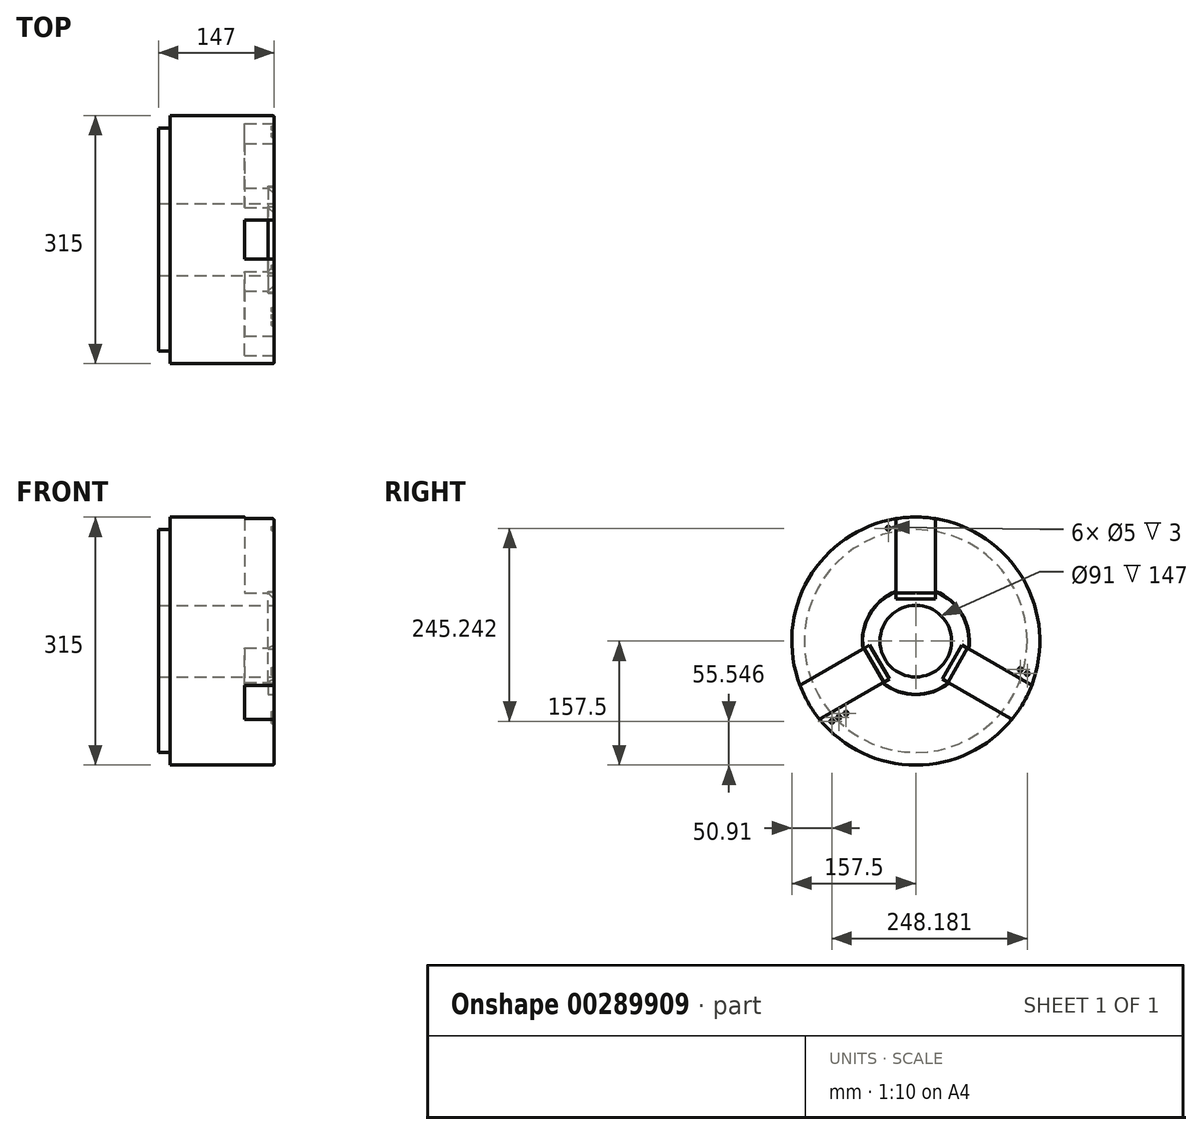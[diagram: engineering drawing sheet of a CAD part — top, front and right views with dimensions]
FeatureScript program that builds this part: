
annotation { "Feature Type Name" : "Feature", "Feature Type Description" : "" }
export const myFeature = defineFeature(function(context is Context, id is Id, definition is map)
    precondition{}
    {
        {
            var Q0;
            Q0=qCreatedBy(makeId("Front.planeOp"),FACE);
            var sketch = newSketch(context, id + "F0", { "sketchPlane" : qUnion([Q0])});
            skLineSegment(sketch, "E0", {"start": v(0, 45.5) * mm, "end": v(0, 67.5) * mm});
            skLineSegment(sketch, "E1", {"start": v(-2, 157.5) * mm, "end": v(-132, 157.5) * mm});
            skLineSegment(sketch, "E2", {"start": v(-132, 157.5) * mm, "end": v(-132, 141.5) * mm});
            skLineSegment(sketch, "E3", {"start": v(-132, 141.5) * mm, "end": v(-147, 141.5) * mm});
            skLineSegment(sketch, "E4", {"start": v(-147, 141.5) * mm, "end": v(-147, 45.5) * mm});
            skLineSegment(sketch, "E5", {"start": v(-147, 45.5) * mm, "end": v(0, 45.5) * mm});
            skLineSegment(sketch, "E6", {"start": v(294.82, 0) * mm, "end": v(-412.28, 0) * mm, "construction": true});
            skPoint(sketch, "E7.visualSharp", {"position": v(0, 157.5) * mm});
            skArc(sketch, "E7.filletArc", {"start": v(0, 155.5) * mm, "mid": v(-0.59, 156.91) * mm, "end": v(-2, 157.5) * mm});
            skLineSegment(sketch, "E8.bottom", {"start": v(0, 67.5) * mm, "end": v(-8, 67.5) * mm});
            skLineSegment(sketch, "E8.top", {"start": v(0, 68) * mm, "end": v(-8, 68) * mm});
            skLineSegment(sketch, "E8.right", {"start": v(-8, 67.5) * mm, "end": v(-8, 68) * mm});
            skLineSegment(sketch, "E9.trimOffspring", {"start": v(0, 68) * mm, "end": v(0, 155.5) * mm});
            skSolve(sketch);
        }
        {
            var Q0;
            Q0=qSketchRegion(id+"F0",true);
            var Q1;
            Q1=sQuery(id+"F0.wireOp",EDGE,"E6");
            revolve(context, id + "F1", {"entities" : qUnion([Q0]), "axis" : qUnion([Q1]), "revolveType" : RevolveType.FULL});
        }
        {
            var Q0;
            Q0=makeQuery(id+"F1.opRevolve","SWEPT_FACE",FACE,{"disambiguationData":[OSD([sQuery(id+"F0.wireOp",EDGE,"E0")])]});
            var sketch = newSketch(context, id + "F2", { "sketchPlane" : qUnion([Q0])});
            skLineSegment(sketch, "E10", {"start": v(0, 0) * mm, "end": v(0, 187.03) * mm, "construction": true});
            skArc(sketch, "E11", {"start": v(25, 155.5) * mm, "mid": v(0, 157.5) * mm, "end": v(-25, 155.5) * mm});
            skPoint(sketch, "E12", {"position": v(0, 62.16) * mm});
            skLineSegment(sketch, "E13", {"start": v(25, 155.5) * mm, "end": v(25, 60.5) * mm});
            skLineSegment(sketch, "E14", {"start": v(25, 60.5) * mm, "end": v(-25, 60.5) * mm});
            skLineSegment(sketch, "E15", {"start": v(-25, 60.5) * mm, "end": v(-25, 155.5) * mm});
            skSolve(sketch);
        }
        {
            var Q0;
            {var subQ0=sQuery(id+"F2.wireOp",EDGE,"E11");Q0=makeQuery(id+"F2.imprint","IMPRINT",FACE,{"disambiguationData":[TD([[makeQuery(id+"F2.imprint","IMPRINT",EDGE,{"derivedFrom":subQ0}),1.0]])]});}
            var Q1;
            {var subQ0=sQuery(id+"F2.wireOp",EDGE,"LmhPQE9t-ctvD-aCPM-Uwr9-EQLkLqq6skGc.bottom");Q1=makeQuery(id+"F2.imprint","IMPRINT",FACE,{"disambiguationData":[TD([[makeQuery(id+"F2.imprint","IMPRINT",EDGE,{"derivedFrom":subQ0}),-1.0]])]});}
            var Q2;
            {var subQ0=sQuery(id+"F2.wireOp",EDGE,"LmhPQE9t-ctvD-aCPM-Uwr9-EQLkLqq6skGc.bottom");var subQ1=makeQuery(id+"F1.opRevolve","SWEPT_EDGE",EDGE,{"disambiguationData":[OSD([sQuery(id+"F0.wireOp",EDGE,"E0"),sQuery(id+"F0.wireOp",EDGE,"E8.bottom")])]});var subQ2=makeQuery(id+"F2.imprint","INTERSECT",VERTEX,{"disambiguationData":[OD(0.0)],"derivedFrom":[subQ1,subQ0]});Q2=makeQuery(id+"F2.imprint","IMPRINT",FACE,{"disambiguationData":[TD([[makeQuery(id+"F2.imprint","IMPRINT",EDGE,{"disambiguationData":[TD([[subQ2,-1.0]])],"derivedFrom":subQ0}),-1.0]])]});}
            extrude(context, id + "F3", {"entities" : qUnion([Q0, Q1, Q2]), "operationType" : NewBodyOperationType.REMOVE, "oppositeDirection" : true, "depth" : 37.5 * mm});
        }
        {
            var Q0;
            Q0=makeQuery(id+"F1.opRevolve","SWEPT_FACE",FACE,{"disambiguationData":[OSD([sQuery(id+"F0.wireOp",EDGE,"E0")])]});
            var sketch = newSketch(context, id + "F4", { "sketchPlane" : qUnion([Q0])});
            skLineSegment(sketch, "E16", {"start": v(25, 73.3) * mm, "end": v(-25, 73.3) * mm});
            skLineSegment(sketch, "E17", {"start": v(-25, 73.3) * mm, "end": v(-25, 53.3) * mm});
            skLineSegment(sketch, "E18", {"start": v(-25, 53.3) * mm, "end": v(25, 53.3) * mm});
            skLineSegment(sketch, "E19", {"start": v(25, 53.3) * mm, "end": v(25, 73.3) * mm});
            skSolve(sketch);
        }
        {
            var Q0;
            Q0=qSketchRegion(id+"F4",true);
            extrude(context, id + "F5", {"entities" : qUnion([Q0]), "operationType" : NewBodyOperationType.REMOVE, "oppositeDirection" : true, "depth" : 8 * mm});
        }
        {
            var Q0;
            Q0=makeQuery(id+"F5.boolean.opBoolean","COPY",EDGE,{"derivedFrom":makeQuery(id+"F5.opExtrude","CAP_EDGE",EDGE,{"disambiguationData":[OSD([sQuery(id+"F4.wireOp",EDGE,"E18")])],"isStart":false})});
            chamfer(context, id + "F6", {"entities" : qUnion([Q0]), "width" : 8 * mm, "tangentPropagation" : true});
        }
        {
            var Q0;
            Q0=makeQuery(id+"F5.boolean.opBoolean","COPY",FACE,{"derivedFrom":makeQuery(id+"F5.opExtrude","CAP_FACE",FACE,{"disambiguationData":[OSD([sQuery(id+"F4.wireOp",EDGE,"E16"),sQuery(id+"F4.wireOp",EDGE,"E17"),sQuery(id+"F4.wireOp",EDGE,"E18"),sQuery(id+"F4.wireOp",EDGE,"E19")])],"isStart":false})});
            var Q1;
            Q1=makeQuery(id+"F3.boolean.opBoolean","COPY",FACE,{"derivedFrom":makeQuery(id+"F3.opExtrude","CAP_FACE",FACE,{"disambiguationData":[OSD([sQuery(id+"F0.wireOp",EDGE,"E0"),sQuery(id+"F0.wireOp",EDGE,"E8.bottom"),sQuery(id+"F2.wireOp",EDGE,"E11"),sQuery(id+"F2.wireOp",EDGE,"E13"),sQuery(id+"F2.wireOp",EDGE,"E15")])],"isStart":false})});
            extrude(context, id + "F7", {"entities" : qUnion([Q0]), "operationType" : NewBodyOperationType.REMOVE, "endBound" : BoundingType.UP_TO_SURFACE, "oppositeDirection" : true, "endBoundEntityFace" : qUnion([Q1]), "depth" : 25 * mm});
        }
        {
            var Q0;
            Q0=makeQuery(id+"F6.opChamfer","BLEND_FACE",FACE,{"disambiguationData":[OSD([sQuery(id+"F4.wireOp",EDGE,"E18")])]});
            var Q1;
            {var subQ0=sQuery(id+"F4.wireOp",EDGE,"E19");Q1=makeQuery(id+"F7.boolean.opBoolean","MERGE",FACE,{"derivedFrom":[makeQuery(id+"F3.boolean.opBoolean","COPY",FACE,{"derivedFrom":makeQuery(id+"F3.opExtrude","SWEPT_FACE",FACE,{"disambiguationData":[OSD([sQuery(id+"F2.wireOp",EDGE,"E13")])]})}),makeQuery(id+"F5.boolean.opBoolean","COPY",FACE,{"derivedFrom":makeQuery(id+"F5.opExtrude","SWEPT_FACE",FACE,{"disambiguationData":[OSD([subQ0])]})})],"fromTools":[makeQuery(id+"F7.opExtrude","SWEPT_FACE",FACE,{"disambiguationData":[OSD([subQ0])]})]});}
            var Q2;
            Q2=makeQuery(id+"F7.boolean.opBoolean","COPY",FACE,{"derivedFrom":makeQuery(id+"F7.opExtrude","SWEPT_FACE",FACE,{"disambiguationData":[OSD([sQuery(id+"F4.wireOp",EDGE,"E16"),sQuery(id+"F4.wireOp",EDGE,"E17"),sQuery(id+"F4.wireOp",EDGE,"E18"),sQuery(id+"F4.wireOp",EDGE,"E19")])]})});
            var Q3;
            Q3=makeQuery(id+"F7.boolean.opBoolean","MERGE",FACE,{"derivedFrom":[makeQuery(id+"F3.boolean.opBoolean","COPY",FACE,{"derivedFrom":makeQuery(id+"F3.opExtrude","CAP_FACE",FACE,{"disambiguationData":[OSD([sQuery(id+"F0.wireOp",EDGE,"E0"),sQuery(id+"F0.wireOp",EDGE,"E8.bottom"),sQuery(id+"F2.wireOp",EDGE,"E11"),sQuery(id+"F2.wireOp",EDGE,"E13"),sQuery(id+"F2.wireOp",EDGE,"E15")])],"isStart":false})})],"fromTools":[makeQuery(id+"F7.opExtrude","CAP_FACE",FACE,{"disambiguationData":[OSD([sQuery(id+"F4.wireOp",EDGE,"E16"),sQuery(id+"F4.wireOp",EDGE,"E17"),sQuery(id+"F4.wireOp",EDGE,"E18"),sQuery(id+"F4.wireOp",EDGE,"E19")])],"isStart":false})]});
            var Q4;
            {var subQ0=sQuery(id+"F4.wireOp",EDGE,"E17");Q4=makeQuery(id+"F7.boolean.opBoolean","MERGE",FACE,{"derivedFrom":[makeQuery(id+"F3.boolean.opBoolean","COPY",FACE,{"derivedFrom":makeQuery(id+"F3.opExtrude","SWEPT_FACE",FACE,{"disambiguationData":[OSD([sQuery(id+"F2.wireOp",EDGE,"E15")])]})}),makeQuery(id+"F5.boolean.opBoolean","COPY",FACE,{"derivedFrom":makeQuery(id+"F5.opExtrude","SWEPT_FACE",FACE,{"disambiguationData":[OSD([subQ0])]})})],"fromTools":[makeQuery(id+"F7.opExtrude","SWEPT_FACE",FACE,{"disambiguationData":[OSD([subQ0])]})]});}
            var Q5;
            Q5=makeQuery(id+"F1.opRevolve","SWEPT_FACE",FACE,{"disambiguationData":[OSD([sQuery(id+"F0.wireOp",EDGE,"E5")])]});
            circularPattern(context, id + "F8", {"patternType" : PatternType.FACE, "operationType" : NewBodyOperationType.ADD, "faces" : qUnion([Q0, Q1, Q2, Q3, Q4]), "axis" : qUnion([Q5]), "angle" : 360 * degree, "instanceCount" : 3, "equalSpace" : true});
        }
        {
            var Q0;
            Q0=makeQuery(id+"F1.opRevolve","SWEPT_FACE",FACE,{"disambiguationData":[OSD([sQuery(id+"F0.wireOp",EDGE,"E0")])]});
            var sketch = newSketch(context, id + "F9", { "sketchPlane" : qUnion([Q0])});
            skCircle(sketch, "E20", {"center": v(-35, 143.29) * mm, "radius": 2.5 * mm});
            skCircle(sketch, "E21", {"center": v(0, 0) * mm, "radius": 147.5 * mm, "construction": true});
            skCircle(sketch, "E22", {"center": v(0, 0) * mm, "radius": 137.5 * mm, "construction": true});
            skCircle(sketch, "E23", {"center": v(0, 0) * mm, "radius": 127.5 * mm, "construction": true});
            skCircle(sketch, "E24", {"center": v(141.6, -41.33) * mm, "radius": 2.5 * mm});
            skCircle(sketch, "E25", {"center": v(132.66, -36.17) * mm, "radius": 2.5 * mm});
            skCircle(sketch, "E26", {"center": v(-106.6, -101.95) * mm, "radius": 2.5 * mm});
            skCircle(sketch, "E27", {"center": v(-97.66, -96.8) * mm, "radius": 2.5 * mm});
            skCircle(sketch, "E28", {"center": v(-88.68, -91.61) * mm, "radius": 2.5 * mm});
            skLineSegment(sketch, "E29", {"start": v(-35, 143.29) * mm, "end": v(-35, 107.8) * mm, "construction": true});
            skLineSegment(sketch, "E30", {"start": v(0, 107.8) * mm, "end": v(0, 150.74) * mm, "construction": true});
            skCircle(sketch, "E31.MirrorC", {"center": v(35, 143.29) * mm, "radius": 2.5 * mm});
            skLineSegment(sketch, "E32", {"start": v(141.6, -41.33) * mm, "end": v(110.08, -23.14) * mm, "construction": true});
            skLineSegment(sketch, "E33", {"start": v(0, 0) * mm, "end": v(131.49, -75.91) * mm, "construction": true});
            skCircle(sketch, "E34.MirrorC", {"center": v(97.66, -96.8) * mm, "radius": 2.5 * mm});
            skCircle(sketch, "E35.MirrorC", {"center": v(106.6, -101.95) * mm, "radius": 2.5 * mm});
            skLineSegment(sketch, "E36", {"start": v(0, 0) * mm, "end": v(-132.86, -76.7) * mm, "construction": true});
            skLineSegment(sketch, "E37", {"start": v(-106.6, -101.95) * mm, "end": v(-83.53, -88.64) * mm, "construction": true});
            skCircle(sketch, "E38.MirrorC", {"center": v(-123.68, -31) * mm, "radius": 2.5 * mm});
            skCircle(sketch, "E39.MirrorC", {"center": v(-132.66, -36.17) * mm, "radius": 2.5 * mm});
            skCircle(sketch, "E40.MirrorC", {"center": v(-141.6, -41.33) * mm, "radius": 2.5 * mm});
            skSolve(sketch);
        }
        {
            var Q0;
            Q0=makeQuery(id+"F9.imprint","IMPRINT",FACE,{"disambiguationData":[TD([[makeQuery(id+"F9.imprint","IMPRINT",EDGE,{"derivedFrom":sQuery(id+"F9.wireOp",EDGE,"E40.MirrorC")}),-1.0]])]});
            var Q1;
            Q1=makeQuery(id+"F9.imprint","IMPRINT",FACE,{"disambiguationData":[TD([[makeQuery(id+"F9.imprint","IMPRINT",EDGE,{"derivedFrom":sQuery(id+"F9.wireOp",EDGE,"E39.MirrorC")}),-1.0]])]});
            var Q2;
            Q2=makeQuery(id+"F9.imprint","IMPRINT",FACE,{"disambiguationData":[TD([[makeQuery(id+"F9.imprint","IMPRINT",EDGE,{"derivedFrom":sQuery(id+"F9.wireOp",EDGE,"E38.MirrorC")}),-1.0]])]});
            var Q3;
            Q3=makeQuery(id+"F9.imprint","IMPRINT",FACE,{"disambiguationData":[TD([[makeQuery(id+"F9.imprint","IMPRINT",EDGE,{"derivedFrom":sQuery(id+"F9.wireOp",EDGE,"E28")}),1.0]])]});
            var Q4;
            Q4=makeQuery(id+"F9.imprint","IMPRINT",FACE,{"disambiguationData":[TD([[makeQuery(id+"F9.imprint","IMPRINT",EDGE,{"derivedFrom":sQuery(id+"F9.wireOp",EDGE,"E27")}),1.0]])]});
            var Q5;
            Q5=makeQuery(id+"F9.imprint","IMPRINT",FACE,{"disambiguationData":[TD([[makeQuery(id+"F9.imprint","IMPRINT",EDGE,{"derivedFrom":sQuery(id+"F9.wireOp",EDGE,"E26")}),1.0]])]});
            var Q6;
            Q6=makeQuery(id+"F9.imprint","IMPRINT",FACE,{"disambiguationData":[TD([[makeQuery(id+"F9.imprint","IMPRINT",EDGE,{"derivedFrom":sQuery(id+"F9.wireOp",EDGE,"E34.MirrorC")}),-1.0]])]});
            var Q7;
            Q7=makeQuery(id+"F9.imprint","IMPRINT",FACE,{"disambiguationData":[TD([[makeQuery(id+"F9.imprint","IMPRINT",EDGE,{"derivedFrom":sQuery(id+"F9.wireOp",EDGE,"E35.MirrorC")}),-1.0]])]});
            var Q8;
            Q8=makeQuery(id+"F9.imprint","IMPRINT",FACE,{"disambiguationData":[TD([[makeQuery(id+"F9.imprint","IMPRINT",EDGE,{"derivedFrom":sQuery(id+"F9.wireOp",EDGE,"E24")}),1.0]])]});
            var Q9;
            Q9=makeQuery(id+"F9.imprint","IMPRINT",FACE,{"disambiguationData":[TD([[makeQuery(id+"F9.imprint","IMPRINT",EDGE,{"derivedFrom":sQuery(id+"F9.wireOp",EDGE,"E25")}),1.0]])]});
            var Q10;
            Q10=makeQuery(id+"F9.imprint","IMPRINT",FACE,{"disambiguationData":[TD([[makeQuery(id+"F9.imprint","IMPRINT",EDGE,{"derivedFrom":sQuery(id+"F9.wireOp",EDGE,"E31.MirrorC")}),-1.0]])]});
            var Q11;
            Q11=makeQuery(id+"F9.imprint","IMPRINT",FACE,{"disambiguationData":[TD([[makeQuery(id+"F9.imprint","IMPRINT",EDGE,{"derivedFrom":sQuery(id+"F9.wireOp",EDGE,"E20")}),1.0]])]});
            var Q12;
            Q12=sQuery(id+"F9.wireOp",EDGE,"E20");
            var Q13;
            Q13=sQuery(id+"F9.wireOp",EDGE,"E31.MirrorC");
            var Q14;
            Q14=sQuery(id+"F9.wireOp",EDGE,"E25");
            var Q15;
            Q15=sQuery(id+"F9.wireOp",EDGE,"E24");
            var Q16;
            Q16=sQuery(id+"F9.wireOp",EDGE,"E35.MirrorC");
            var Q17;
            Q17=sQuery(id+"F9.wireOp",EDGE,"E34.MirrorC");
            var Q18;
            Q18=sQuery(id+"F9.wireOp",EDGE,"E28");
            var Q19;
            Q19=sQuery(id+"F9.wireOp",EDGE,"E27");
            var Q20;
            Q20=sQuery(id+"F9.wireOp",EDGE,"E26");
            var Q21;
            Q21=sQuery(id+"F9.wireOp",EDGE,"E38.MirrorC");
            var Q22;
            Q22=sQuery(id+"F9.wireOp",EDGE,"E39.MirrorC");
            var Q23;
            Q23=sQuery(id+"F9.wireOp",EDGE,"E40.MirrorC");
            extrude(context, id + "F10", {"entities" : qUnion([Q0, Q1, Q2, Q3, Q4, Q5, Q6, Q7, Q8, Q9, Q10, Q11]), "operationType" : NewBodyOperationType.REMOVE, "surfaceEntities" : qUnion([Q12, Q13, Q14, Q15, Q16, Q17, Q18, Q19, Q20, Q21, Q22, Q23]), "oppositeDirection" : true, "depth" : 3 * mm});
        }
    });
